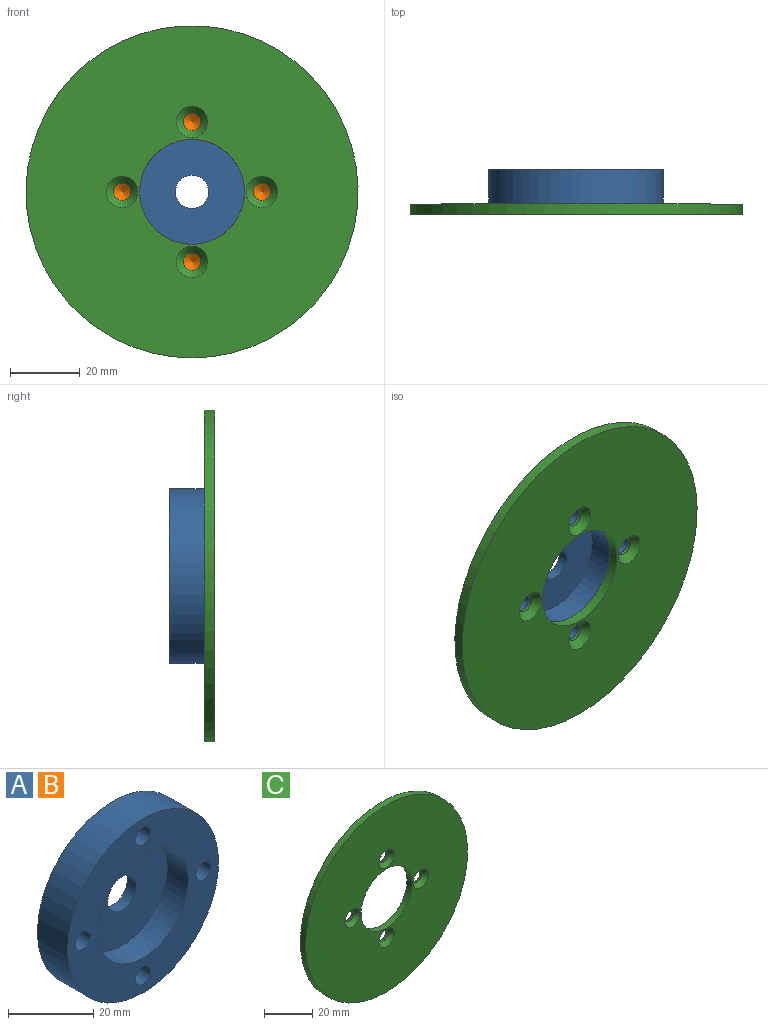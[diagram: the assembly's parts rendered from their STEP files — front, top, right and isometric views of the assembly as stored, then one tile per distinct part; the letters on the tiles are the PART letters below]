
ASSEMBLY  parts=3 mates=1
PART A: 14 faces, bbox 50x10x50 mm
  f0: cylinder r=4.75mm len=9.5mm, axis (0,-1,0), area 89.5mm2, adj f3,f4
  f1: cylinder r=25mm len=50mm, axis (0,1,0), area 1570.8mm2, adj f2,f3
  f2: plane 50x50mm, normal (0,-1,0), area 1178.1mm2, adj f1,f5,f7,f9,f11,f13
  f3: plane 50x50mm, normal (0,1,0), area 1892.6mm2, adj f0,f1
  f4: plane 30x30mm, normal (0,-1,0), area 636mm2, adj f0,f5
  f5: cylinder r=15mm len=30mm, axis (0,-1,0), area 659.7mm2, adj f2,f4
  f6: cone r=0mm half-angle=59deg, axis (0,-1,0), area 22.9mm2, adj f7
  f7: cylinder r=2.5mm len=6mm, axis (0,-1,0), area 94.2mm2, adj f2,f6
  f8: cone r=0mm half-angle=59deg, axis (0,-1,0), area 22.9mm2, adj f9
  f9: cylinder r=2.5mm len=6mm, axis (0,-1,0), area 94.2mm2, adj f2,f8
  f10: cone r=0mm half-angle=59deg, axis (0,-1,0), area 22.9mm2, adj f11
  f11: cylinder r=2.5mm len=6mm, axis (0,-1,0), area 94.2mm2, adj f2,f10
  f12: cone r=0mm half-angle=59deg, axis (0,-1,0), area 22.9mm2, adj f13
  f13: cylinder r=2.5mm len=6mm, axis (0,-1,0), area 94.2mm2, adj f2,f12
PART B: same geometry as A
PART C: 12 faces, bbox 95x3x95 mm
  f0: cylinder r=47.5mm len=95mm, axis (0,1,0), area 895.4mm2, adj f1,f2
  f1: plane 95x95mm, normal (0,-1,0), area 6126.9mm2, adj f0,f3,f8,f9,f10,f11
  f2: plane 95x95mm, normal (0,1,0), area 6302.8mm2, adj f0,f3,f4,f5,f6,f7
  f3: cylinder r=15mm len=30mm, axis (0,-1,0), area 282.7mm2, adj f1,f2
  f4: cylinder r=2.5mm len=5mm, axis (0,-1,0), area 15.7mm2, adj f2,f11
  f5: cylinder r=2.5mm len=5mm, axis (0,-1,0), area 15.7mm2, adj f2,f9
  f6: cylinder r=2.5mm len=5mm, axis (0,-1,0), area 15.7mm2, adj f2,f8
  f7: cylinder r=2.5mm len=5mm, axis (0,-1,0), area 15.7mm2, adj f2,f10
  f8: cone r=2.5mm half-angle=45deg, axis (0,-1,0), area 62.2mm2, adj f1,f6
  f9: cone r=2.5mm half-angle=45deg, axis (0,-1,0), area 62.2mm2, adj f1,f5
  f10: cone r=2.5mm half-angle=45deg, axis (0,-1,0), area 62.2mm2, adj f1,f7
  f11: cone r=2.5mm half-angle=45deg, axis (0,-1,0), area 62.2mm2, adj f1,f4
PLACE A t=(16.25,16.47,3.14)mm
PLACE B t=(16.25,16.47,3.14)mm
PLACE C t=(16.25,6.47,3.14)mm
MATE cylindrical C.f3 <-> A.f0  axis (0,1,0) through (16.25,6.47,3.14)mm
